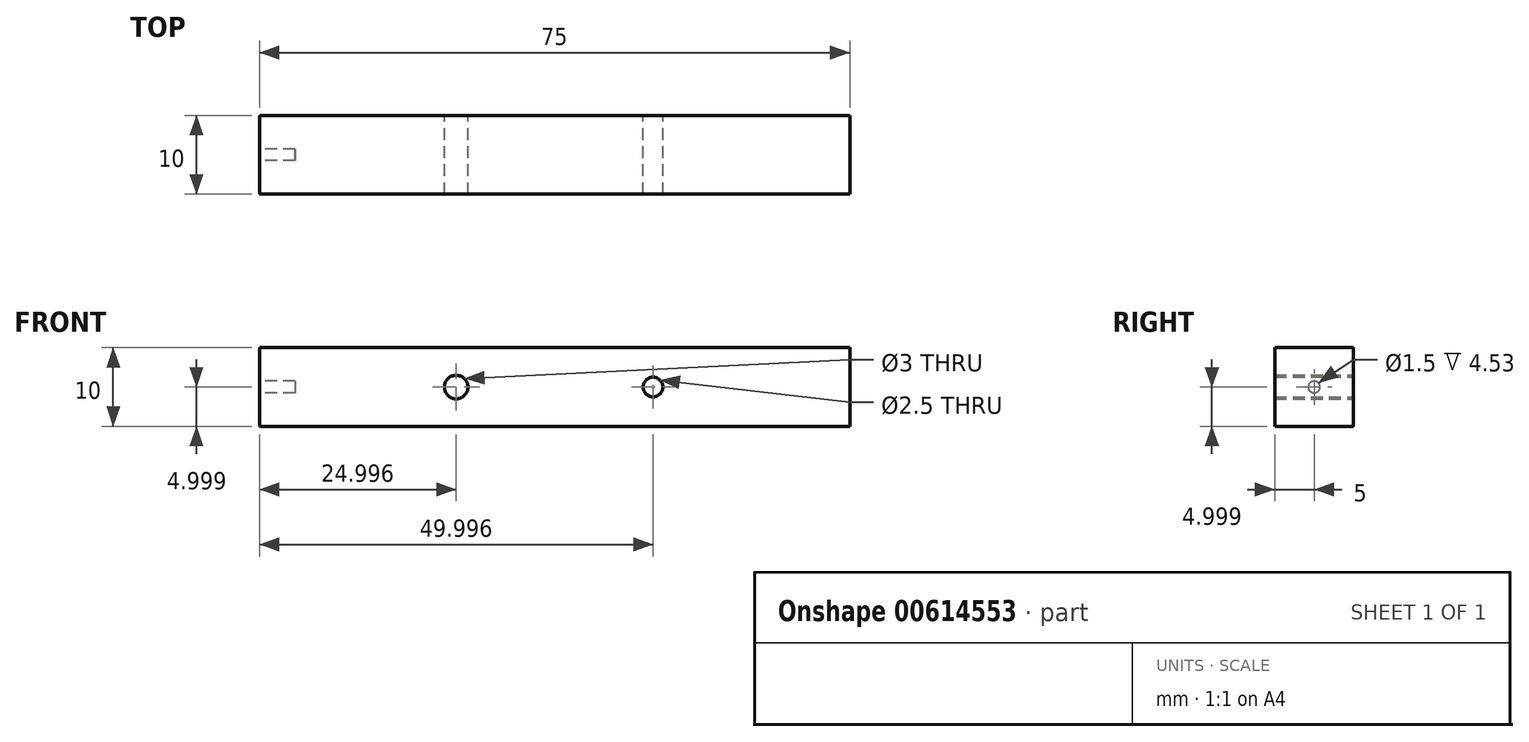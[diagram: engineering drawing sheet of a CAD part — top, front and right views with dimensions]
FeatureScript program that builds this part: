
annotation { "Feature Type Name" : "Feature", "Feature Type Description" : "" }
export const myFeature = defineFeature(function(context is Context, id is Id, definition is map)
    precondition{}
    {
        {
            var Q0;
            Q0=qCreatedBy(makeId("Front.planeOp"),FACE);
            var sketch = newSketch(context, id + "F0", { "sketchPlane" : qUnion([Q0])});
            skLineSegment(sketch, "E0.bottom", {"start": v(-12.98, 6.65) * mm, "end": v(62.02, 6.65) * mm});
            skLineSegment(sketch, "E0.top", {"start": v(-12.98, -3.35) * mm, "end": v(62.02, -3.35) * mm});
            skLineSegment(sketch, "E0.left", {"start": v(-12.98, 6.65) * mm, "end": v(-12.98, -3.35) * mm});
            skLineSegment(sketch, "E0.right", {"start": v(62.02, 6.65) * mm, "end": v(62.02, -3.35) * mm});
            skCircle(sketch, "E1", {"center": v(12.02, 1.65) * mm, "radius": 1.5 * mm});
            skCircle(sketch, "E2", {"center": v(37.02, 1.65) * mm, "radius": 1.25 * mm});
            skSolve(sketch);
        }
        {
            var Q0;
            Q0=makeQuery(id+"F0.imprint","IMPRINT",FACE,{"disambiguationData":[TD([[makeQuery(id+"F0.imprint","IMPRINT",EDGE,{"derivedFrom":sQuery(id+"F0.wireOp",EDGE,"E0.bottom")}),-1.0]])]});
            extrude(context, id + "F1", {"entities" : qUnion([Q0]), "endBound" : BoundingType.SYMMETRIC, "depth" : 10 * mm, "offsetDistance" : 25 * mm});
        }
        {
            var Q0;
            Q0=makeQuery(id+"F1.opExtrude","SWEPT_FACE",FACE,{"disambiguationData":[OSD([sQuery(id+"F0.wireOp",EDGE,"E0.left")])]});
            var sketch = newSketch(context, id + "F2", { "sketchPlane" : qUnion([Q0])});
            skCircle(sketch, "E3", {"center": v(0, 1.65) * mm, "radius": 0.75 * mm});
            skSolve(sketch);
        }
        {
            var Q0;
            Q0=makeQuery(id+"F2.imprint","IMPRINT",FACE,{"disambiguationData":[TD([[makeQuery(id+"F2.imprint","IMPRINT",EDGE,{"derivedFrom":sQuery(id+"F2.wireOp",EDGE,"E3")}),1.0]])]});
            extrude(context, id + "F3", {"entities" : qUnion([Q0]), "operationType" : NewBodyOperationType.REMOVE, "endBound" : BoundingType.SYMMETRIC, "oppositeDirection" : true, "depth" : 9.06 * mm, "offsetDistance" : 25 * mm});
        }
    });
